# Revit family: Accessory-Tissue_Holder-KOHLER-Avid-K-97502BR_1
name_source: partatom
category: Specialty Equipment
revit_build: Autodesk Revit 2017 (Build: 20160225_1515(x64)
units: mm (PartAtom-declared; Revit-internal decimal feet)

## family parameters
Cut with Voids When Loaded = No
Host = Face
OmniClass Number = 23.31.25.21
OmniClass Title = Toilet Paper Dispensers
Part Type = Normal
Room Calculation Point = No
Round Connector Dimension = Use Diameter
Shared = No

## types (4) — shared parameters
ADA Compliant = No
Assembly Code = C1030200
Date Modified = 05/24/2021
Default Elevation = 42"
Description = Vertical paper bin
Height = 5 13/16"
Length = 5 1/16"
Manufacturer = KOHLER Co.
Master Format 2014 = 10 28 00
Master Format 2014 Name = Toilet, Bath, and Laundry Accessories
Material = Premium metal construction
Product Documentation Link = http://resources.kohler.com
Product Name = AVID
Product Page URL = https://www.br.kohler.com
URL = https://br.kohler.com
WaterSense Certified = No
Width = 1 3/4"

## per-type parameters (varying)
| type | Finish | Model | Type |
| CP-Polished Chrome | Kohler-Metal-CP-Polished_Chrome | K-97502BR-CP | 1 |
| TT-Titanium Silver | Kohler-Metal-TT-Titanium_Silver | K-97502BR-TT | 2 |
| BN-Vibrant Brushed Nickel | Kohler-Metal-BN-Vibrant_Brushed_Nickel | K-97502BR-BN | 3 |
| RGD-Polished Rose Gold | Kohler-Metal-RGD-Polished_Rose_Gold | K-97502BR-RGD | 4 |

## geometry (parser evidence)
native form markers: Sweep x5
no freeform markers — native parametric forms only
